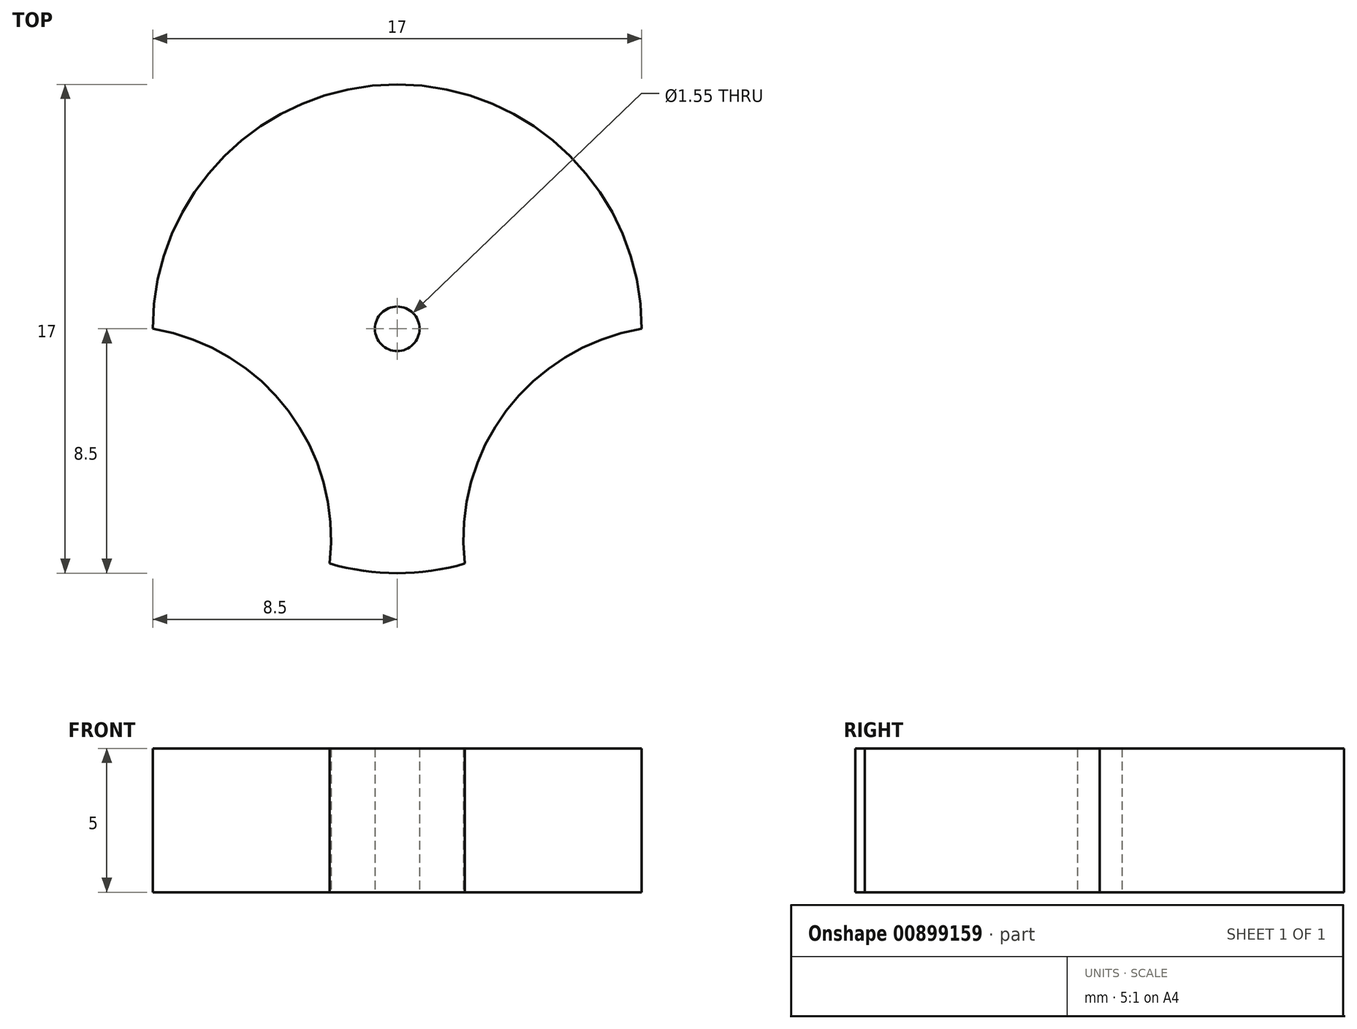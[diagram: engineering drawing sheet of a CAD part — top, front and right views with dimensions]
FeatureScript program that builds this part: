
annotation { "Feature Type Name" : "Feature", "Feature Type Description" : "" }
export const myFeature = defineFeature(function(context is Context, id is Id, definition is map)
    precondition{}
    {
        {
            var Q0;
            Q0=qCreatedBy(makeId("Top.planeOp"),FACE);
            var sketch = newSketch(context, id + "F0", { "sketchPlane" : qUnion([Q0])});
            skCircle(sketch, "E0", {"center": v(0, 0) * mm, "radius": 2.5 * mm, "construction": true});
            skCircle(sketch, "E1", {"center": v(0, 0) * mm, "radius": 0.78 * mm});
            skArc(sketch, "E2", {"start": v(-2.35, -8.17) * mm, "mid": v(0, -8.5) * mm, "end": v(2.35, -8.17) * mm});
            skCircle(sketch, "E3", {"center": v(0, 0) * mm, "radius": 12.5 * mm, "construction": true});
            skLineSegment(sketch, "E4.bottom", {"start": v(-2.35, -8.17) * mm, "end": v(2.35, -8.17) * mm, "construction": true});
            skLineSegment(sketch, "E4.top", {"start": v(-2.35, 8.17) * mm, "end": v(2.35, 8.17) * mm, "construction": true});
            skLineSegment(sketch, "E4.left", {"start": v(-2.35, -8.17) * mm, "end": v(-2.35, 8.17) * mm, "construction": true});
            skLineSegment(sketch, "E4.right", {"start": v(2.35, -8.17) * mm, "end": v(2.35, 8.17) * mm, "construction": true});
            skLineSegment(sketch, "E5.bottom", {"start": v(-16.8, -9.42) * mm, "end": v(16.8, -9.42) * mm, "construction": true});
            skLineSegment(sketch, "E5.top", {"start": v(-16.8, 9.42) * mm, "end": v(16.8, 9.42) * mm, "construction": true});
            skLineSegment(sketch, "E5.left", {"start": v(-16.8, -9.42) * mm, "end": v(-16.8, 9.42) * mm, "construction": true});
            skLineSegment(sketch, "E5.right", {"start": v(16.8, -9.42) * mm, "end": v(16.8, 9.42) * mm, "construction": true});
            skArc(sketch, "E6", {"start": v(-12.5, -0.45) * mm, "mid": v(-15.61, -11.75) * mm, "end": v(-3.89, -11.88) * mm, "construction": true});
            skPoint(sketch, "E6.first.point", {"position": v(-8.5, 0) * mm});
            skArc(sketch, "E7", {"start": v(8.5, 0) * mm, "mid": v(3.79, -2.85) * mm, "end": v(2.35, -8.17) * mm});
            skPoint(sketch, "E7.first.point", {"position": v(8.5, 0) * mm});
            skPoint(sketch, "E8", {"position": v(0, -8.5) * mm});
            skPoint(sketch, "E9", {"position": v(0, 8.5) * mm});
            skPoint(sketch, "E9.positionSnap0", {"position": v(0, 8.17) * mm});
            skArc(sketch, "E10.trimOffspring", {"start": v(8.5, 0) * mm, "mid": v(0, 8.5) * mm, "end": v(-8.5, 0) * mm});
            skArc(sketch, "E11.trimOffspring", {"start": v(-2.35, -8.17) * mm, "mid": v(-3.79, -2.85) * mm, "end": v(-8.5, 0) * mm});
            skArc(sketch, "E12.trimOffspring", {"start": v(3.89, -11.88) * mm, "mid": v(15.61, -11.75) * mm, "end": v(12.5, -0.45) * mm, "construction": true});
            skSolve(sketch);
        }
        {
            var Q0;
            Q0=makeQuery(id+"F0.imprint","IMPRINT",FACE,{"disambiguationData":[TD([[makeQuery(id+"F0.imprint","IMPRINT",EDGE,{"derivedFrom":sQuery(id+"F0.wireOp",EDGE,"E1")}),-1.0]])]});
            extrude(context, id + "F1", {"entities" : qUnion([Q0]), "depth" : 5 * mm, "offsetDistance" : 25 * mm});
        }
    });
